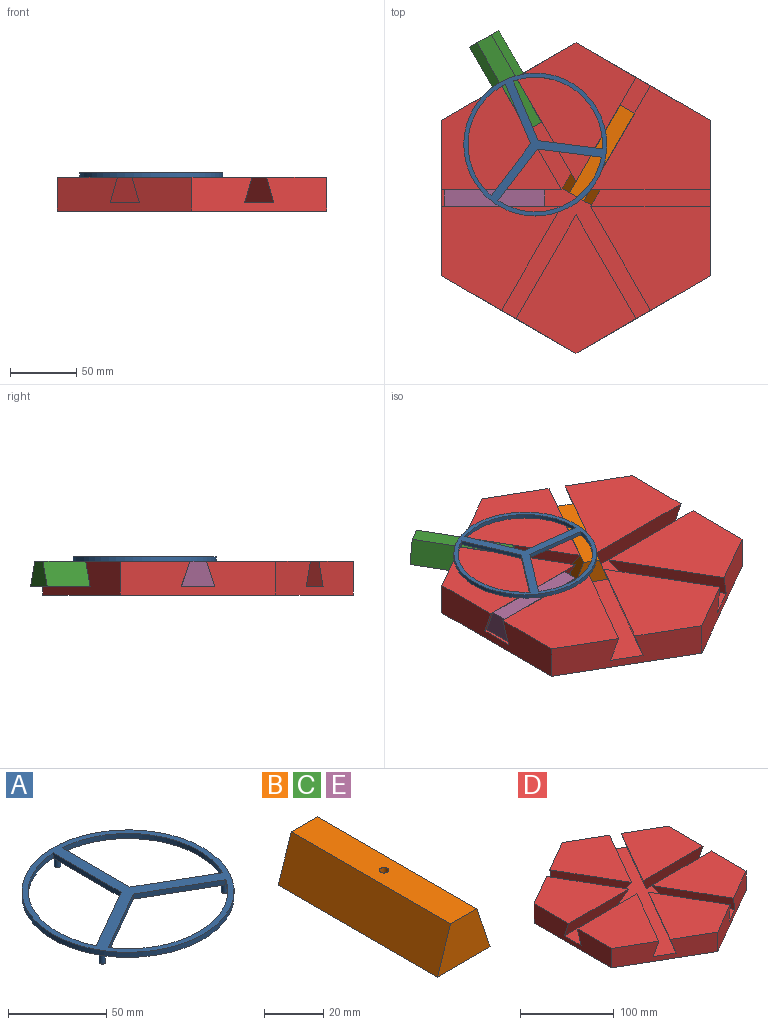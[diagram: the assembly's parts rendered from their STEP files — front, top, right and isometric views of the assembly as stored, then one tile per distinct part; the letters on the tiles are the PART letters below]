
ASSEMBLY  parts=5 mates=6
PART A: 18 faces, bbox 108x108x9.7 mm
  f0: plane 48.87x3.18mm, normal (-1,0,0), area 155.2mm2, adj f2,f3,f8,f16
  f1: plane 48.87x3.18mm, normal (1,0,0), area 155.2mm2, adj f2,f3,f6,f15
  f2: plane 107.95x107.95mm, normal (0,0,1), area 1994.7mm2, adj f0,f1,f6,f7,f8,f11,f14,f15
  f3: plane 107.95x107.95mm, normal (0,0,-1), area 1971mm2, adj f0,f1,f4,f6,f7,f8,f9,f11
  f4: cylinder r=1.59mm len=6.48mm, axis (0,0,1), area 64.6mm2, adj f3,f5
  f5: plane 3.18x3.18mm, normal (0,0,-1), area 7.9mm2, adj f4
  f6: plane 42.32x24.43mm, normal (0.5,0.87,0), area 155.2mm2, adj f1,f2,f3,f15
  f7: plane 42.32x24.43mm, normal (0.5,-0.87,0), area 155.2mm2, adj f2,f3,f11,f17
  f8: plane 42.32x24.43mm, normal (-0.5,0.87,0), area 155.2mm2, adj f0,f2,f3,f16
  f9: cylinder r=1.59mm len=6.48mm, axis (0,0,1), area 64.6mm2, adj f3,f10
  f10: plane 3.18x3.18mm, normal (0,0,-1), area 7.9mm2, adj f9
  f11: plane 42.32x24.43mm, normal (-0.5,-0.87,0), area 155.2mm2, adj f2,f3,f7,f17
  f12: cylinder r=1.59mm len=6.48mm, axis (0,0,1), area 64.6mm2, adj f3,f13
  f13: plane 3.18x3.18mm, normal (0,0,-1), area 7.9mm2, adj f12
  f14: cylinder r=53.98mm len=107.95mm, axis (0,0,-1), area 1076.8mm2, adj f2,f3
  f15: cylinder r=50.8mm len=73.3mm, axis (0,0,-1), area 317.6mm2, adj f1,f2,f3,f6
  f16: cylinder r=50.8mm len=73.3mm, axis (0,0,-1), area 317.6mm2, adj f0,f2,f3,f8
  f17: cylinder r=50.8mm len=84.64mm, axis (0,0,-1), area 317.6mm2, adj f2,f3,f7,f11
PART B: 8 faces, bbox 25.1x76.2x18.9 mm
  f0: plane 76.2x25.15mm, normal (0,0,-1), area 1916.1mm2, adj f1,f3,f4,f5
  f1: plane 76.2x18.92mm, normal (0.95,0,0.32), area 1521mm2, adj f0,f2,f4,f5
  f2: plane 76.2x12.45mm, normal (0,0,1), area 940.5mm2, adj f1,f3,f4,f5,f6
  f3: plane 76.2x18.92mm, normal (-0.95,0,0.32), area 1521mm2, adj f0,f2,f4,f5
  f4: plane 25.15x18.92mm, normal (0,-1,0), area 355.7mm2, adj f0,f1,f2,f3
  f5: plane 25.15x18.92mm, normal (0,1,0), area 355.7mm2, adj f0,f1,f2,f3
  f6: cylinder r=1.59mm len=6.35mm, axis (0,0,1), area 63.3mm2, adj f2,f7
  f7: plane 3.18x3.18mm, normal (0,0,1), area 7.9mm2, adj f6
PART C: same geometry as B
PART D: 26 faces, bbox 203.2x234.6x25.4 mm
  f0: plane 90.6x78.46mm, normal (0,0,1), area 4739.3mm2, adj f8,f13,f19,f24
  f1: plane 90.6x78.46mm, normal (0,0,1), area 4739.3mm2, adj f7,f14,f22,f23
  f2: plane 104.62x90.6mm, normal (0,0,1), area 4739.3mm2, adj f11,f12,f23,f24
  f3: plane 104.62x90.6mm, normal (0,0,1), area 4739.3mm2, adj f16,f18,f20,f21
  f4: plane 90.6x78.46mm, normal (0,0,1), area 4739.3mm2, adj f9,f17,f21,f22
  f5: plane 90.6x78.46mm, normal (0,0,1), area 4739.3mm2, adj f6,f15,f19,f20
  f6: plane 90.6x19.05mm, normal (0,-0.95,-0.32), area 1708.9mm2, adj f5,f10,f15,f19
  f7: plane 90.6x19.05mm, normal (0,0.95,-0.32), area 1708.9mm2, adj f1,f10,f14,f22
  f8: plane 90.6x19.05mm, normal (0,0.95,-0.32), area 1708.9mm2, adj f0,f10,f13,f19
  f9: plane 90.6x19.05mm, normal (0,-0.95,-0.32), area 1708.9mm2, adj f4,f10,f17,f22
  f10: plane 203.2x188.68mm, normal (0,0,1), area 13807.7mm2, adj f6,f7,f8,f9,f11,f12,f13,f14
  f11: plane 81.64x45.3mm, normal (-0.82,0.47,-0.32), area 1708.9mm2, adj f2,f10,f12,f24
  f12: plane 81.64x45.3mm, normal (0.82,0.47,-0.32), area 1708.9mm2, adj f2,f10,f11,f23
  f13: plane 78.46x50.8mm, normal (0.82,-0.47,-0.32), area 1708.9mm2, adj f0,f8,f10,f24
  f14: plane 78.46x50.8mm, normal (-0.82,-0.47,-0.32), area 1708.9mm2, adj f1,f7,f10,f23
  f15: plane 78.46x50.8mm, normal (0.82,0.47,-0.32), area 1708.9mm2, adj f5,f6,f10,f20
  f16: plane 81.64x45.3mm, normal (-0.82,-0.47,-0.32), area 1708.9mm2, adj f3,f10,f18,f20
  f17: plane 78.46x50.8mm, normal (-0.82,0.47,-0.32), area 1708.9mm2, adj f4,f9,f10,f21
  f18: plane 81.64x45.3mm, normal (0.82,-0.47,-0.32), area 1708.9mm2, adj f3,f10,f16,f21
  f19: plane 117.32x25.4mm, normal (-1,0,0), area 2617mm2, adj f0,f5,f6,f8,f10,f20,f24,f25
  f20: plane 101.6x58.66mm, normal (-0.5,0.87,0), area 2617mm2, adj f3,f5,f10,f15,f16,f19,f21,f25
  f21: plane 101.6x58.66mm, normal (0.5,0.87,0), area 2617mm2, adj f3,f4,f10,f17,f18,f20,f22,f25
  f22: plane 117.32x25.4mm, normal (1,0,0), area 2617mm2, adj f1,f4,f7,f9,f10,f21,f23,f25
  f23: plane 101.6x58.66mm, normal (0.5,-0.87,0), area 2617mm2, adj f1,f2,f10,f12,f14,f22,f24,f25
  f24: plane 101.6x58.66mm, normal (-0.5,-0.87,0), area 2617mm2, adj f0,f2,f10,f11,f13,f19,f23,f25
  f25: plane 234.64x203.2mm, normal (0,0,-1), area 35758.4mm2, adj f19,f20,f21,f22,f23,f24
PART E: same geometry as B
PLACE A rot(axis=(0,0,1),22.7deg) t=(-30.76,40.43,25.6)mm
PLACE B rot(axis=(0,0,-1),30deg) t=(19.64,34.01,6.55)mm
PLACE C rot(axis=(0,0,1),30deg) t=(-50.39,87.28,6.55)mm
PLACE D at identity fixed
PLACE E rot(axis=(0,0,1),90deg) t=(-61.51,0,6.55)mm
MATE revolute A.f12 <-> B.f6  axis (0,0,-1) through (19.64,34.01,19.12)mm
MATE revolute A.f4 <-> C.f6  axis (0,0,-1) through (-50.39,87.28,19.12)mm
MATE slider E.f5 <-> D.f19  axis (-1,0,0) through (-99.61,0,14.95)mm
MATE slider C.f4 <-> D.f23  axis (0.5,-0.87,0) through (-31.34,54.29,14.95)mm
MATE revolute A.f9 <-> E.f6  axis (0,0,-1) through (-61.51,0,19.12)mm
MATE slider B.f4 <-> D.f24  axis (-0.5,-0.87,0) through (0.59,1.02,14.95)mm
